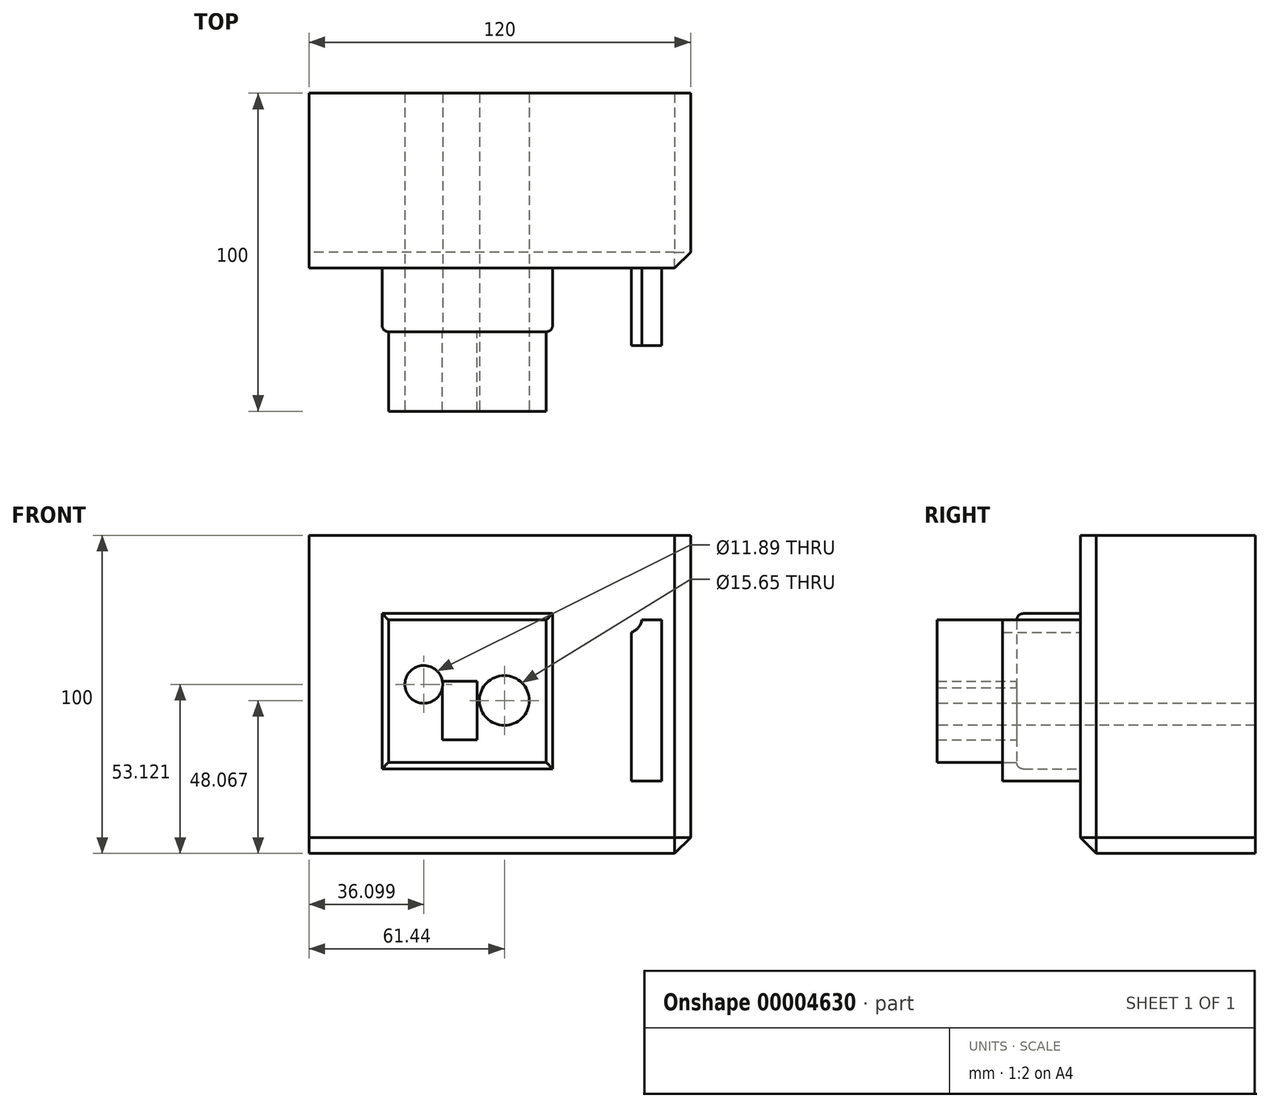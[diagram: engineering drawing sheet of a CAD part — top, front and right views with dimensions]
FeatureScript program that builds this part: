
annotation { "Feature Type Name" : "Feature", "Feature Type Description" : "" }
export const myFeature = defineFeature(function(context is Context, id is Id, definition is map)
    precondition{}
    {
        {
            var Q0;
            Q0=qCreatedBy(makeId("Front.planeOp"),FACE);
            var sketch = newSketch(context, id + "F0", { "sketchPlane" : qUnion([Q0])});
            skLineSegment(sketch, "E0.bottom", {"start": v(-61.44, 56.3) * mm, "end": v(58.56, 56.3) * mm});
            skLineSegment(sketch, "E0.top", {"start": v(-61.44, -43.7) * mm, "end": v(58.56, -43.7) * mm});
            skLineSegment(sketch, "E0.left", {"start": v(-61.44, 56.3) * mm, "end": v(-61.44, -43.7) * mm});
            skLineSegment(sketch, "E0.right", {"start": v(58.56, 56.3) * mm, "end": v(58.56, -43.7) * mm});
            skSolve(sketch);
        }
        {
            var Q0;
            Q0 = qSketchRegion(id + "F0", true);
            extrude(context, id + "F1", {"entities" : qUnion([Q0]), "flatOperationType" : FlatOperationType.REMOVE, "depth" : 55 * mm, "offsetDistance" : 25 * mm, "domain" : OperationDomain.MODEL});
        }
        {
            var Q0;
            Q0=makeQuery(id+"F1.opExtrude","CAP_FACE",FACE,{"disambiguationData":[OSD([sQuery(id+"F0.wireOp",EDGE,"E0.bottom"),sQuery(id+"F0.wireOp",EDGE,"E0.top"),sQuery(id+"F0.wireOp",EDGE,"E0.left"),sQuery(id+"F0.wireOp",EDGE,"E0.right")])],"isStart":false});
            var sketch = newSketch(context, id + "F2", { "sketchPlane" : qUnion([Q0])});
            skLineSegment(sketch, "E1.bottom", {"start": v(-38.44, 31.7) * mm, "end": v(15.18, 31.7) * mm});
            skLineSegment(sketch, "E1.top", {"start": v(-38.44, -17.14) * mm, "end": v(15.18, -17.14) * mm});
            skLineSegment(sketch, "E1.left", {"start": v(-38.44, 31.7) * mm, "end": v(-38.44, -17.14) * mm});
            skLineSegment(sketch, "E1.right", {"start": v(15.18, 31.7) * mm, "end": v(15.18, -17.14) * mm});
            skSolve(sketch);
        }
        {
            var Q0;
            Q0=makeQuery(id+"F2.imprint","IMPRINT",FACE,{"disambiguationData":[TD([[makeQuery(id+"F2.imprint","IMPRINT",EDGE,{"derivedFrom":sQuery(id+"F2.wireOp",EDGE,"E1.bottom")}),-1.0]])]});
            extrude(context, id + "F3", {"entities" : qUnion([Q0]), "operationType" : NewBodyOperationType.ADD, "depth" : 20 * mm});
        }
        {
            var Q0;
            Q0=makeQuery(id+"F3.opExtrude","CAP_FACE",FACE,{"disambiguationData":[OSD([sQuery(id+"F2.wireOp",EDGE,"E1.bottom"),sQuery(id+"F2.wireOp",EDGE,"E1.top"),sQuery(id+"F2.wireOp",EDGE,"E1.left"),sQuery(id+"F2.wireOp",EDGE,"E1.right")])],"isStart":false});
            fillet(context, id + "F4", {"entities" : qUnion([Q0]), "radius" : 2 * mm, "tangentPropagation" : true, "allowEdgeOverflow" : false});
        }
        {
            var Q0;
            Q0=makeQuery(id+"F1.opExtrude","CAP_FACE",FACE,{"disambiguationData":[OSD([sQuery(id+"F0.wireOp",EDGE,"E0.bottom"),sQuery(id+"F0.wireOp",EDGE,"E0.top"),sQuery(id+"F0.wireOp",EDGE,"E0.left"),sQuery(id+"F0.wireOp",EDGE,"E0.right")])],"isStart":false});
            var sketch = newSketch(context, id + "F5", { "sketchPlane" : qUnion([Q0])});
            skCircle(sketch, "E2", {"center": v(38.56, 30.3) * mm, "radius": 4.68 * mm});
            skSolve(sketch);
        }
        {
            var Q0;
            Q0=makeQuery(id+"F1.opExtrude","SWEPT_EDGE",EDGE,{"disambiguationData":[OSD([sQuery(id+"F0.wireOp",EDGE,"E0.top"),sQuery(id+"F0.wireOp",EDGE,"E0.right")])]});
            var Q1;
            Q1=makeQuery(id+"F1.opExtrude","CAP_EDGE",EDGE,{"disambiguationData":[OSD([sQuery(id+"F0.wireOp",EDGE,"E0.top")])],"isStart":false});
            var Q2;
            Q2=makeQuery(id+"F1.opExtrude","CAP_EDGE",EDGE,{"disambiguationData":[OSD([sQuery(id+"F0.wireOp",EDGE,"E0.right")])],"isStart":false});
            chamfer(context, id + "F6", {"entities" : qUnion([Q0, Q1, Q2]), "width" : 5 * mm, "tangentPropagation" : true});
        }
        {
            var Q0;
            Q0=makeQuery(id+"F5.imprint","IMPRINT",FACE,{"disambiguationData":[TD([[makeQuery(id+"F5.imprint","IMPRINT",EDGE,{"derivedFrom":sQuery(id+"F5.wireOp",EDGE,"E2")}),-1.0]])]});
            var sketch = newSketch(context, id + "F7", { "sketchPlane" : qUnion([Q0])});
            skLineSegment(sketch, "E3.bottom", {"start": v(39.95, 29.74) * mm, "end": v(49.4, 29.74) * mm});
            skLineSegment(sketch, "E3.top", {"start": v(39.95, -20.98) * mm, "end": v(49.4, -20.98) * mm});
            skLineSegment(sketch, "E3.left", {"start": v(39.95, 29.74) * mm, "end": v(39.95, -20.98) * mm});
            skLineSegment(sketch, "E3.right", {"start": v(49.4, 29.74) * mm, "end": v(49.4, -20.98) * mm});
            skSolve(sketch);
        }
        {
            var Q0;
            {var subQ6=sQuery(id+"F7.wireOp",EDGE,"E3.top");Q0=makeQuery(id+"F7.imprint","IMPRINT",FACE,{"disambiguationData":[TD([[makeQuery(id+"F7.imprint","IMPRINT",EDGE,{"derivedFrom":subQ6}),1.0]])]});}
            extrude(context, id + "F8", {"entities" : qUnion([Q0]), "operationType" : NewBodyOperationType.ADD, "depth" : 24.4 * mm});
        }
        {
            var Q0;
            Q0=makeQuery(id+"F3.opExtrude","CAP_FACE",FACE,{"disambiguationData":[OSD([sQuery(id+"F2.wireOp",EDGE,"E1.bottom"),sQuery(id+"F2.wireOp",EDGE,"E1.top"),sQuery(id+"F2.wireOp",EDGE,"E1.left"),sQuery(id+"F2.wireOp",EDGE,"E1.right")])],"isStart":false});
            var sketch = newSketch(context, id + "F9", { "sketchPlane" : qUnion([Q0])});
            skCircle(sketch, "E4", {"center": v(0, 4.37) * mm, "radius": 7.82 * mm});
            skCircle(sketch, "E5", {"center": v(-25.34, 9.42) * mm, "radius": 5.94 * mm});
            skSolve(sketch);
        }
        {
            var Q0;
            Q0=makeQuery(id+"F9.imprint","IMPRINT",FACE,{"disambiguationData":[TD([[makeQuery(id+"F9.imprint","IMPRINT",EDGE,{"derivedFrom":sQuery(id+"F9.wireOp",EDGE,"E4")}),1.0]])]});
            var Q1;
            Q1=makeQuery(id+"F9.imprint","IMPRINT",FACE,{"disambiguationData":[TD([[makeQuery(id+"F9.imprint","IMPRINT",EDGE,{"derivedFrom":sQuery(id+"F9.wireOp",EDGE,"E5")}),1.0]])]});
            extrude(context, id + "F10", {"entities" : qUnion([Q0, Q1]), "operationType" : NewBodyOperationType.REMOVE, "endBound" : BoundingType.THROUGH_ALL, "oppositeDirection" : true, "depth" : 25 * mm, "offsetDistance" : 25 * mm});
        }
        {
            var Q0;
            Q0=makeQuery(id+"F3.opExtrude","CAP_FACE",FACE,{"disambiguationData":[OSD([sQuery(id+"F2.wireOp",EDGE,"E1.bottom"),sQuery(id+"F2.wireOp",EDGE,"E1.top"),sQuery(id+"F2.wireOp",EDGE,"E1.left"),sQuery(id+"F2.wireOp",EDGE,"E1.right")])],"isStart":false});
            var sketch = newSketch(context, id + "F11", { "sketchPlane" : qUnion([Q0])});
            skLineSegment(sketch, "E6.bottom", {"start": v(-19.49, 10.45) * mm, "end": v(-8.52, 10.45) * mm});
            skLineSegment(sketch, "E6.top", {"start": v(-19.49, -7.96) * mm, "end": v(-8.52, -7.96) * mm});
            skLineSegment(sketch, "E6.left", {"start": v(-19.49, 10.45) * mm, "end": v(-19.49, -7.96) * mm});
            skLineSegment(sketch, "E6.right", {"start": v(-8.52, 10.45) * mm, "end": v(-8.52, -7.96) * mm});
            skSolve(sketch);
        }
        {
            var Q0;
            {var subQ4=sQuery(id+"F11.wireOp",EDGE,"E6.bottom");Q0=makeQuery(id+"F11.imprint","IMPRINT",FACE,{"disambiguationData":[TD([[makeQuery(id+"F11.imprint","IMPRINT",EDGE,{"derivedFrom":subQ4}),1.0]])]});}
            extrude(context, id + "F12", {"entities" : qUnion([Q0]), "operationType" : NewBodyOperationType.ADD, "depth" : 25 * mm, "offsetDistance" : 25 * mm});
        }
    });
